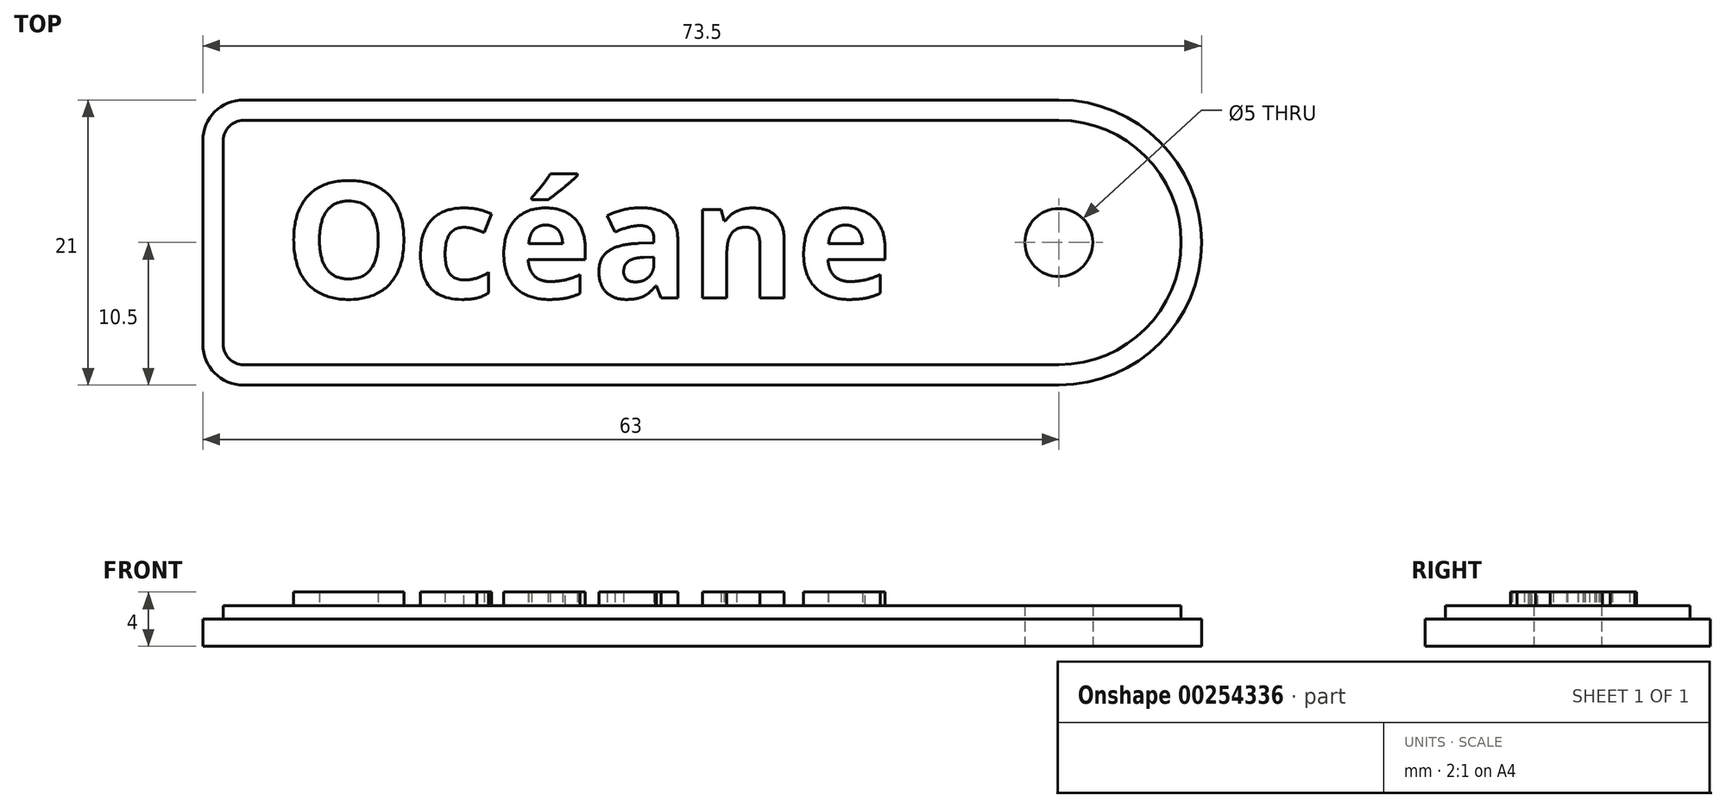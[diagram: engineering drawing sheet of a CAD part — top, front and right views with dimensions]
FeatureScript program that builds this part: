
annotation { "Feature Type Name" : "Feature", "Feature Type Description" : "" }
export const myFeature = defineFeature(function(context is Context, id is Id, definition is map)
    precondition{}
    {
        {
            var Q0;
            Q0=qCreatedBy(makeId("Top.planeOp"),FACE);
            var sketch = newSketch(context, id + "F0", { "sketchPlane" : qUnion([Q0])});
            skLineSegment(sketch, "E0.bottom", {"start": v(3, -10.5) * mm, "end": v(63, -10.5) * mm});
            skLineSegment(sketch, "E0.top", {"start": v(3, 10.5) * mm, "end": v(63, 10.5) * mm});
            skArc(sketch, "E1", {"start": v(63, 10.5) * mm, "mid": v(73.5, 0) * mm, "end": v(63, -10.5) * mm});
            skCircle(sketch, "E2", {"center": v(63, 0) * mm, "radius": 2.5 * mm});
            skLineSegment(sketch, "E3", {"start": v(0, 7.5) * mm, "end": v(0, -7.5) * mm});
            skPoint(sketch, "E4.visualSharp", {"position": v(0, 10.5) * mm});
            skArc(sketch, "E4.filletArc", {"start": v(3, 10.5) * mm, "mid": v(0.88, 9.62) * mm, "end": v(0, 7.5) * mm});
            skPoint(sketch, "E5.visualSharp", {"position": v(0, -10.5) * mm});
            skArc(sketch, "E5.filletArc", {"start": v(0, -7.5) * mm, "mid": v(0.88, -9.62) * mm, "end": v(3, -10.5) * mm});
            skSolve(sketch);
        }
        {
            var Q0;
            Q0 = qSketchRegion(id + "F0", true);
            extrude(context, id + "F1", {"entities" : qUnion([Q0]), "depth" : 3 * mm});
        }
        {
            var Q0;
            Q0=makeQuery(id+"F1.opExtrude","CAP_FACE",FACE,{"disambiguationData":[OSD([sQuery(id+"F0.wireOp",EDGE,"E0.bottom"),sQuery(id+"F0.wireOp",EDGE,"E0.top"),sQuery(id+"F0.wireOp",EDGE,"E1"),sQuery(id+"F0.wireOp",EDGE,"E2"),sQuery(id+"F0.wireOp",EDGE,"E3"),sQuery(id+"F0.wireOp",EDGE,"E4.filletArc"),sQuery(id+"F0.wireOp",EDGE,"E5.filletArc")])],"isStart":false});
            var sketch = newSketch(context, id + "F2", { "sketchPlane" : qUnion([Q0])});
            skText(sketch, "E6", { "text": "Océane\n", "fontName": "OpenSans-Bold.ttf"});
            const initialGuessF2  = {"E6": [0.006, -0.00408, 1, 0, 0.00858]};
            skSetInitialGuess(sketch, initialGuessF2);
            skSolve(sketch);
        }
        {
            var Q0;
            Q0 = qSketchRegion(id + "F2", true);
            extrude(context, id + "F3", {"entities" : qUnion([Q0]), "operationType" : NewBodyOperationType.ADD, "depth" : 1 * mm});
        }
        {
            var Q0;
            {var subQ0=sQuery(id+"F0.wireOp",EDGE,"E2");var subQ1=sQuery(id+"F0.wireOp",EDGE,"E1");var subQ2=sQuery(id+"F0.wireOp",EDGE,"E0.bottom");var subQ3=sQuery(id+"F0.wireOp",EDGE,"E3");var subQ4=sQuery(id+"F0.wireOp",EDGE,"E4.filletArc");var subQ5=sQuery(id+"F0.wireOp",EDGE,"E5.filletArc");var subQ6=sQuery(id+"F0.wireOp",EDGE,"E0.top");Q0=makeQuery(id+"F3.boolean.opBoolean","SPLIT",FACE,{"disambiguationData":[TD([makeQuery(id+"F1.opExtrude","SWEPT_FACE",FACE,{"disambiguationData":[OSD([subQ2])]})])],"derivedFrom":makeQuery(id+"F1.opExtrude","CAP_FACE",FACE,{"disambiguationData":[OSD([subQ2,subQ6,subQ1,subQ0,subQ3,subQ4,subQ5])],"isStart":false})});}
            var sketch = newSketch(context, id + "F4", { "sketchPlane" : qUnion([Q0])});
            skLineSegment(sketch, "E7.0", {"start": v(3, 9) * mm, "end": v(63, 9) * mm});
            skLineSegment(sketch, "E7.1", {"start": v(3, -9) * mm, "end": v(63, -9) * mm});
            skArc(sketch, "E7.2", {"start": v(1.5, -7.5) * mm, "mid": v(1.94, -8.56) * mm, "end": v(3, -9) * mm});
            skArc(sketch, "E7.3", {"start": v(63, 9) * mm, "mid": v(72, 0) * mm, "end": v(63, -9) * mm});
            skLineSegment(sketch, "E7.4", {"start": v(1.5, 7.5) * mm, "end": v(1.5, -7.5) * mm});
            skArc(sketch, "E7.5", {"start": v(3, 9) * mm, "mid": v(1.94, 8.56) * mm, "end": v(1.5, 7.5) * mm});
            skSolve(sketch);
        }
        {
            var Q0;
            Q0=makeQuery(id+"F4.imprint","IMPRINT",FACE,{"disambiguationData":[TD([[makeQuery(id+"F4.imprint","IMPRINT",EDGE,{"derivedFrom":sQuery(id+"F4.wireOp",EDGE,"E7.0")}),1.0]])]});
            extrude(context, id + "F5", {"entities" : qUnion([Q0]), "operationType" : NewBodyOperationType.REMOVE, "oppositeDirection" : true, "depth" : 1 * mm});
        }
    });
